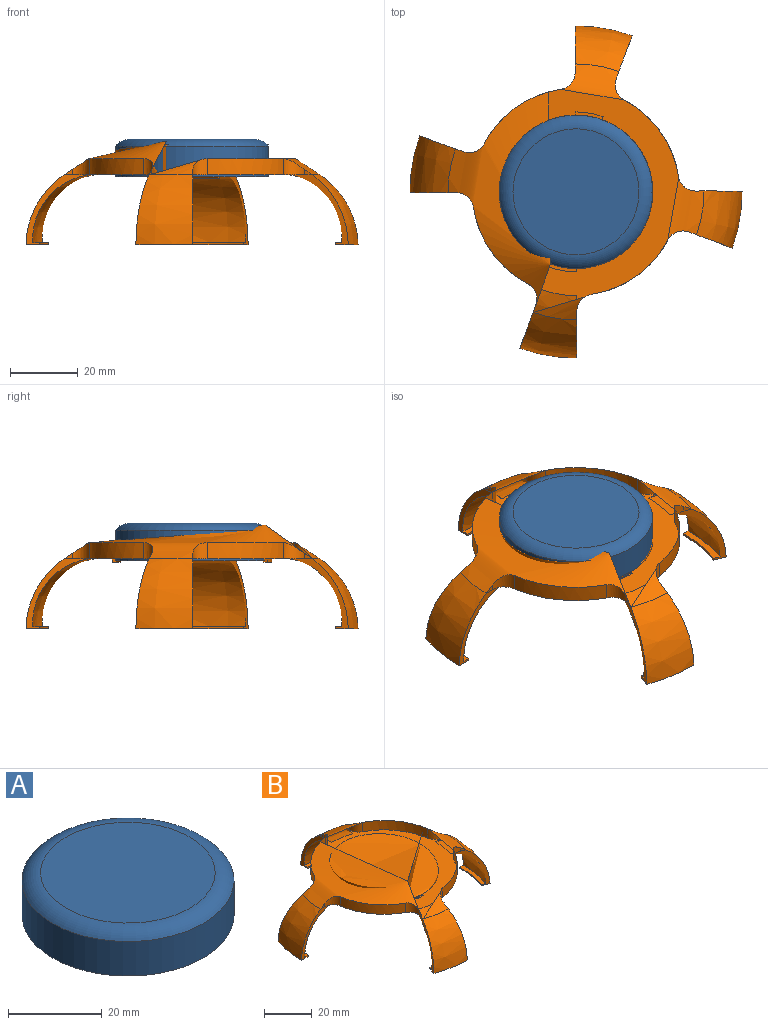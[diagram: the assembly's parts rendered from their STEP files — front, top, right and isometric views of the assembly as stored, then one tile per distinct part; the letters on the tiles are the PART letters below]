
ASSEMBLY  parts=2 mates=1
PART A: 4 faces, bbox 51.1x51.1x11 mm
  f0: plane 45.2x45.2mm, normal (0,0,-1), area 1604.6mm2, adj f1
  f1: cylinder r=22.6mm len=45.2mm, axis (0,0,-1), area 1278mm2, adj f0,f2
  f2: torus R=18.6mm, axis (0,0,-1), area 604.7mm2, adj f1,f3
  f3: plane 37.2x37.2mm, normal (0,0,1), area 1086.9mm2, adj f2
PART B: 69 faces, bbox 101x101x33.5 mm
  f0: revolved ~19.99x18.19mm, area 409.5mm2, adj f1,f66,f67,f68
  f1: plane 23.55x20.21mm, normal (-0.94,0.34,0), area 47.4mm2, adj f0,f2,f3,f64,f65,f66,f68
  f2: revolved ~15.41x2.65mm, area 9.4mm2, adj f1,f65,f66,f67
  f3: plane 2.37x1.68mm, normal (-0.94,0.34,0), area 2.1mm2, adj f1,f4,f44
  f4: cylinder r=5mm len=6.12mm, axis (0,0,1), area 23.2mm2, adj f3,f5,f44,f68
  f5: cylinder r=30.61mm len=22.59mm, axis (0,0,1), area 138.1mm2, adj f4,f6,f44,f68
  f6: cylinder r=5mm len=4.97mm, axis (0,0,1), area 23.2mm2, adj f5,f7,f44,f68
  f7: plane 2.54x1.7mm, normal (0,-1,0), area 2.2mm2, adj f6,f8,f44
  f8: plane 20.61x18.36mm, normal (0,-1,0), area 47.5mm2, adj f7,f9,f40,f41,f42,f43,f68
  f9: revolved ~16.09x4.65mm, area 32.1mm2, adj f8,f10,f40,f43
  f10: plane 23.55x20.19mm, normal (0.34,0.94,0), area 47.5mm2, adj f9,f11,f40,f41,f42,f43,f68
  f11: plane 2.36x1.68mm, normal (0.34,0.94,0), area 2.1mm2, adj f10,f12,f44
  f12: cylinder r=5mm len=6.12mm, axis (0,0,1), area 23.2mm2, adj f11,f13,f44,f68
  f13: cylinder r=30.61mm len=22.59mm, axis (0,0,1), area 138.1mm2, adj f12,f14,f44,f68
  f14: cylinder r=5mm len=4.97mm, axis (0,0,1), area 23.2mm2, adj f13,f15,f44,f68
  f15: plane 2.54x1.7mm, normal (-1,0,0), area 2.2mm2, adj f14,f16,f44
  f16: plane 20.61x18.36mm, normal (-1,0,0), area 47.5mm2, adj f15,f17,f36,f37,f38,f39,f68
  f17: revolved ~16.09x4.65mm, area 32.1mm2, adj f16,f18,f36,f39
  f18: plane 23.55x20.19mm, normal (0.94,-0.34,0), area 47.5mm2, adj f17,f19,f36,f37,f38,f39,f68
  f19: plane 2.36x1.68mm, normal (0.94,-0.34,0), area 2.1mm2, adj f18,f20,f44
  f20: cylinder r=5mm len=6.12mm, axis (0,0,1), area 23.2mm2, adj f19,f21,f44,f68
  f21: cylinder r=30.61mm len=22.59mm, axis (0,0,1), area 138.1mm2, adj f20,f22,f44,f68
  f22: cylinder r=5mm len=4.97mm, axis (0,0,1), area 23.2mm2, adj f21,f23,f44,f68
  f23: plane 2.54x1.7mm, normal (0,1,0), area 2.2mm2, adj f22,f24,f44
  f24: plane 20.61x18.36mm, normal (0,1,0), area 47.5mm2, adj f23,f25,f32,f33,f34,f35,f68
  f25: revolved ~16.09x4.65mm, area 32.1mm2, adj f24,f26,f32,f35
  f26: plane 23.55x20.19mm, normal (-0.34,-0.94,0), area 47.5mm2, adj f25,f27,f32,f33,f34,f35,f68
  f27: plane 2.36x1.68mm, normal (-0.34,-0.94,0), area 2.1mm2, adj f26,f28,f44
  f28: cylinder r=5mm len=6.12mm, axis (0,0,1), area 23.2mm2, adj f27,f29,f44,f68
  f29: cylinder r=30.61mm len=22.59mm, axis (0,0,1), area 138.1mm2, adj f28,f30,f44,f68
  f30: cylinder r=5mm len=4.97mm, axis (0,0,1), area 23.2mm2, adj f29,f31,f44,f68
  f31: plane 2.54x1.7mm, normal (1,0,0), area 2.2mm2, adj f30,f44,f67
  f32: revolved ~15.41x2.65mm, area 9.4mm2, adj f24,f25,f26,f33
  f33: revolved ~16.77x6.65mm, area 65.6mm2, adj f24,f26,f32,f34
  f34: revolved ~20.6x16.82mm, area 383.8mm2, adj f24,f26,f33,f44
  f35: revolved ~19.99x18.14mm, area 409.2mm2, adj f24,f25,f26,f68
  f36: revolved ~15.41x2.65mm, area 9.4mm2, adj f16,f17,f18,f37
  f37: revolved ~16.77x6.65mm, area 65.6mm2, adj f16,f18,f36,f38
  f38: revolved ~20.6x16.82mm, area 383.8mm2, adj f16,f18,f37,f44
  f39: revolved ~19.99x18.14mm, area 409.2mm2, adj f16,f17,f18,f68
  f40: revolved ~15.41x2.65mm, area 9.4mm2, adj f8,f9,f10,f41
  f41: revolved ~16.77x6.65mm, area 65.6mm2, adj f8,f10,f40,f42
  f42: revolved ~20.6x16.82mm, area 383.8mm2, adj f8,f10,f41,f44
  f43: revolved ~19.99x18.14mm, area 409.2mm2, adj f8,f9,f10,f68
  f44: revolved ~75.45x75.45mm, area 1399.4mm2, adj f3,f4,f5,f6,f7,f11,f12,f13
  f45: revolved ~45.61x45.61mm, area 166.7mm2, adj f44,f46
  f46: revolved ~45.23x45.23mm, area 196.8mm2, adj f45,f47
  f47: revolved ~45.29x45.29mm, area 1280.7mm2, adj f46,f48,f54,f55,f56,f62,f63,f68
  f48: plane 1.41x1mm, normal (0.94,-0.34,0), area 1.1mm2, adj f47,f49,f50,f51,f52,f53,f54,f68
  f49: revolved ~8.08x1.42mm, area 8mm2, adj f48,f50,f55,f68
  f50: revolved ~8.07x2.36mm, area 8.1mm2, adj f48,f49,f51,f55
  f51: revolved ~7.73x1.83mm, area 5.5mm2, adj f48,f50,f52,f55
  f52: revolved ~7.73x1.83mm, area 3.9mm2, adj f48,f51,f53,f55
  f53: revolved ~7.73x1.36mm, area 3.9mm2, adj f48,f52,f54,f55
  f54: revolved ~7.75x1.43mm, area 0.5mm2, adj f47,f48,f53,f55
  f55: plane 1.5x1mm, normal (-1,0,0), area 1.1mm2, adj f47,f49,f50,f51,f52,f53,f54,f68
  f56: plane 1.41x1mm, normal (-0.94,0.34,0), area 1.1mm2, adj f47,f57,f58,f59,f60,f61,f62,f68
  f57: revolved ~8.08x1.42mm, area 8mm2, adj f56,f58,f63,f68
  f58: revolved ~8.07x2.36mm, area 8.1mm2, adj f56,f57,f59,f63
  f59: revolved ~7.73x1.83mm, area 5.5mm2, adj f56,f58,f60,f63
  f60: revolved ~7.73x1.83mm, area 3.9mm2, adj f56,f59,f61,f63
  f61: revolved ~7.73x1.36mm, area 3.9mm2, adj f56,f60,f62,f63
  f62: revolved ~7.75x1.43mm, area 0.5mm2, adj f47,f56,f61,f63
  f63: plane 1.5x1mm, normal (1,0,0), area 1.1mm2, adj f47,f57,f58,f59,f60,f61,f62,f68
  f64: revolved ~20.6x16.82mm, area 383.8mm2, adj f1,f44,f65,f67
  f65: revolved ~16.77x6.65mm, area 65.6mm2, adj f1,f2,f64,f67
  f66: revolved ~16.09x4.65mm, area 32.1mm2, adj f0,f1,f2,f67
  f67: plane 20.61x18.38mm, normal (1,0,0), area 47.5mm2, adj f0,f2,f31,f64,f65,f66,f68
  f68: revolved ~70.44x70.44mm, area 1350.9mm2, adj f0,f1,f4,f5,f6,f8,f10,f12
PLACE A t=(-3.87,-11.1,0.9)mm
PLACE B t=(-3.87,-11.1,-18.79)mm
MATE planar A.f1 <-> B.f5  axis (0,0,-1) through (-3.87,-11.1,0.9)mm
